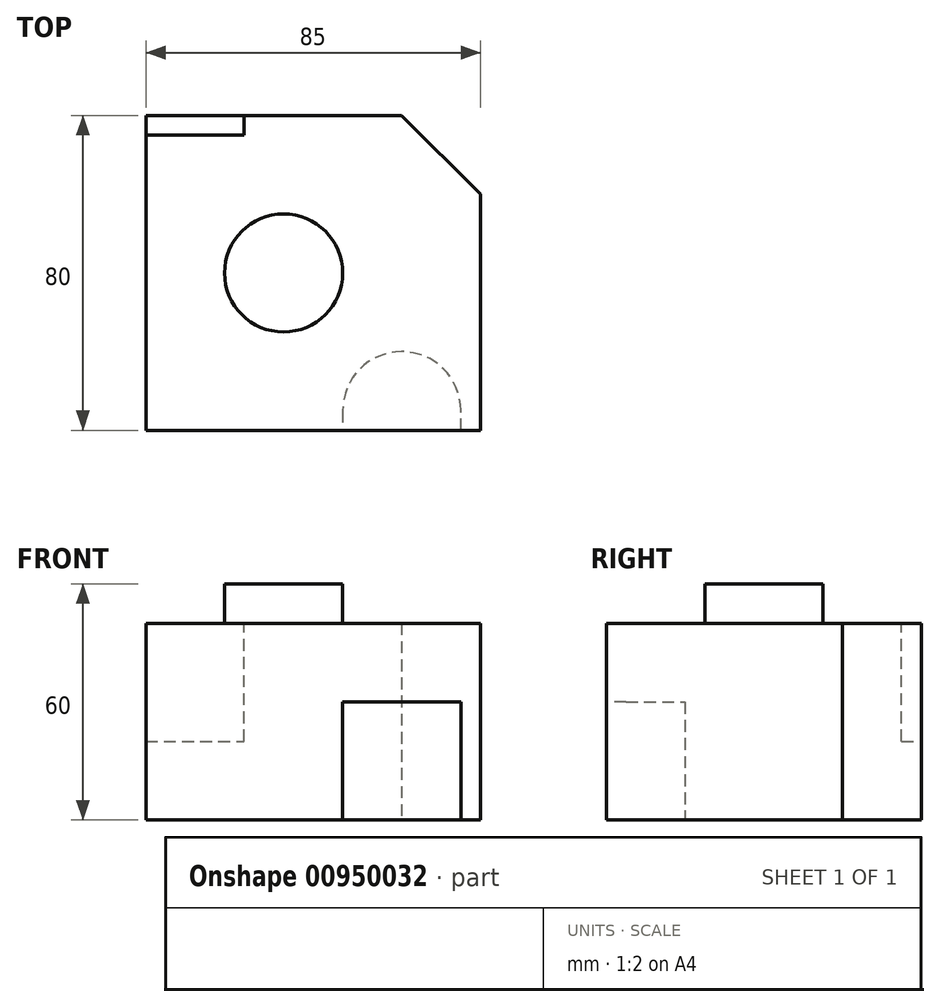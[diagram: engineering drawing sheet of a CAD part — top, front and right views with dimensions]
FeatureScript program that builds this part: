
annotation { "Feature Type Name" : "Feature", "Feature Type Description" : "" }
export const myFeature = defineFeature(function(context is Context, id is Id, definition is map)
    precondition{}
    {
        {
            var Q0;
            Q0=qCreatedBy(makeId("Top.planeOp"),FACE);
            var sketch = newSketch(context, id + "F0", { "sketchPlane" : qUnion([Q0])});
            skLineSegment(sketch, "E0.bottom", {"start": v(0, 0) * mm, "end": v(85, 0) * mm});
            skLineSegment(sketch, "E0.top", {"start": v(0, 80) * mm, "end": v(85, 80) * mm});
            skLineSegment(sketch, "E0.left", {"start": v(0, 0) * mm, "end": v(0, 80) * mm});
            skLineSegment(sketch, "E0.right", {"start": v(85, 0) * mm, "end": v(85, 80) * mm});
            skSolve(sketch);
        }
        {
            var Q0;
            Q0 = qSketchRegion(id + "F0", true);
            extrude(context, id + "F1", {"entities" : qUnion([Q0]), "depth" : 50 * mm, "offsetDistance" : 25 * mm});
        }
        {
            var Q0;
            Q0=makeQuery(id+"F1.opExtrude","SWEPT_EDGE",EDGE,{"disambiguationData":[OSD([sQuery(id+"F0.wireOp",EDGE,"E0.top"),sQuery(id+"F0.wireOp",EDGE,"E0.right")])]});
            chamfer(context, id + "F2", {"entities" : qUnion([Q0]), "width" : 20 * mm, "tangentPropagation" : true});
        }
        {
            var Q0;
            Q0=makeQuery(id+"F1.opExtrude","CAP_FACE",FACE,{"disambiguationData":[OSD([sQuery(id+"F0.wireOp",EDGE,"E0.bottom"),sQuery(id+"F0.wireOp",EDGE,"E0.top"),sQuery(id+"F0.wireOp",EDGE,"E0.left"),sQuery(id+"F0.wireOp",EDGE,"E0.right")])],"isStart":false});
            var sketch = newSketch(context, id + "F3", { "sketchPlane" : qUnion([Q0])});
            skLineSegment(sketch, "E1.bottom", {"start": v(0, 80) * mm, "end": v(25, 80) * mm});
            skLineSegment(sketch, "E1.top", {"start": v(0, 75) * mm, "end": v(25, 75) * mm});
            skLineSegment(sketch, "E1.left", {"start": v(0, 80) * mm, "end": v(0, 75) * mm});
            skLineSegment(sketch, "E1.right", {"start": v(25, 80) * mm, "end": v(25, 75) * mm});
            skSolve(sketch);
        }
        {
            var Q0;
            Q0 = qSketchRegion(id + "F3", true);
            extrude(context, id + "F4", {"entities" : qUnion([Q0]), "operationType" : NewBodyOperationType.REMOVE, "oppositeDirection" : true, "depth" : 30 * mm, "offsetDistance" : 25 * mm});
        }
        {
            var Q0;
            Q0=makeQuery(id+"F1.opExtrude","CAP_FACE",FACE,{"disambiguationData":[OSD([sQuery(id+"F0.wireOp",EDGE,"E0.bottom"),sQuery(id+"F0.wireOp",EDGE,"E0.top"),sQuery(id+"F0.wireOp",EDGE,"E0.left"),sQuery(id+"F0.wireOp",EDGE,"E0.right")])],"isStart":false});
            var sketch = newSketch(context, id + "F5", { "sketchPlane" : qUnion([Q0])});
            skCircle(sketch, "E2", {"center": v(35, 40) * mm, "radius": 15 * mm});
            skSolve(sketch);
        }
        {
            var Q0;
            Q0 = qSketchRegion(id + "F5", true);
            extrude(context, id + "F6", {"entities" : qUnion([Q0]), "operationType" : NewBodyOperationType.ADD, "depth" : 10 * mm, "offsetDistance" : 25 * mm});
        }
        {
            var Q0;
            Q0=makeQuery(id+"F1.opExtrude","CAP_FACE",FACE,{"disambiguationData":[OSD([sQuery(id+"F0.wireOp",EDGE,"E0.bottom"),sQuery(id+"F0.wireOp",EDGE,"E0.top"),sQuery(id+"F0.wireOp",EDGE,"E0.left"),sQuery(id+"F0.wireOp",EDGE,"E0.right")])],"isStart":true});
            var sketch = newSketch(context, id + "F7", { "sketchPlane" : qUnion([Q0])});
            skArc(sketch, "E3", {"start": v(50, -5) * mm, "mid": v(65, -20) * mm, "end": v(80, -5) * mm});
            skLineSegment(sketch, "E4", {"start": v(50, -5) * mm, "end": v(50, 0) * mm});
            skLineSegment(sketch, "E5", {"start": v(50, 0) * mm, "end": v(80, 0) * mm});
            skLineSegment(sketch, "E6", {"start": v(80, 0) * mm, "end": v(80, -5) * mm});
            skSolve(sketch);
        }
        {
            var Q0;
            Q0 = qSketchRegion(id + "F7", true);
            extrude(context, id + "F8", {"entities" : qUnion([Q0]), "operationType" : NewBodyOperationType.REMOVE, "oppositeDirection" : true, "depth" : 30 * mm, "offsetDistance" : 25 * mm});
        }
    });
